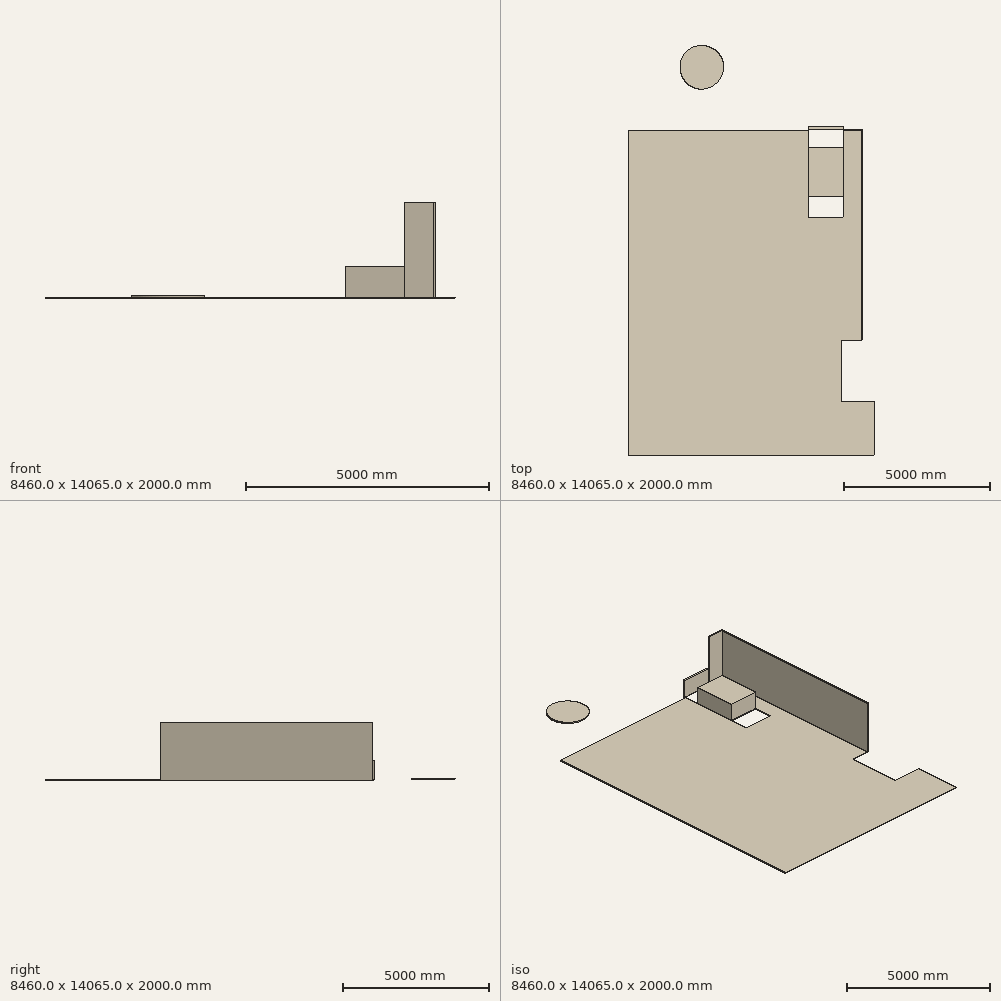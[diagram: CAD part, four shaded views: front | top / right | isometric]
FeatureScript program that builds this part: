
annotation { "Feature Type Name" : "Feature", "Feature Type Description" : "" }
export const myFeature = defineFeature(function(context is Context, id is Id, definition is map)
    precondition{}
    {
        {
            var Q0;
            Q0=qCreatedBy(makeId("Top.planeOp"),FACE);
            var sketch = newSketch(context, id + "F0", { "sketchPlane" : qUnion([Q0])});
            skLineSegment(sketch, "E0", {"start": v(3786.2, -11769.83) * mm, "end": v(3786.2, -9919.83) * mm});
            skLineSegment(sketch, "E1", {"start": v(3786.2, -9919.83) * mm, "end": v(2626.2, -9919.83) * mm});
            skLineSegment(sketch, "E2", {"start": v(2626.2, -9919.83) * mm, "end": v(2626.2, -7819.83) * mm});
            skLineSegment(sketch, "E3", {"start": v(2626.2, -7819.83) * mm, "end": v(3326.2, -7819.83) * mm});
            skLineSegment(sketch, "E4", {"start": v(3326.2, -7819.83) * mm, "end": v(3326.2, -619.83) * mm});
            skLineSegment(sketch, "E5", {"start": v(3326.2, -619.83) * mm, "end": v(-4673.8, -619.83) * mm});
            skLineSegment(sketch, "E6", {"start": v(-4673.8, -619.83) * mm, "end": v(-4673.8, -11769.83) * mm});
            skLineSegment(sketch, "E7", {"start": v(-4673.8, -11769.83) * mm, "end": v(3786.2, -11769.83) * mm});
            skLineSegment(sketch, "E8.bottom", {"start": v(2726.2, -1219.83) * mm, "end": v(1526.2, -1219.83) * mm});
            skLineSegment(sketch, "E8.top", {"start": v(2726.2, -3619.83) * mm, "end": v(1526.2, -3619.83) * mm});
            skLineSegment(sketch, "E8.left", {"start": v(2726.2, -1219.83) * mm, "end": v(2726.2, -3619.83) * mm});
            skLineSegment(sketch, "E8.right", {"start": v(1526.2, -1219.83) * mm, "end": v(1526.2, -3619.83) * mm});
            skLineSegment(sketch, "E9.bottom", {"start": v(2726.2, -492.67) * mm, "end": v(1526.2, -492.67) * mm});
            skLineSegment(sketch, "E9.top", {"start": v(2726.2, -2892.67) * mm, "end": v(1526.2, -2892.67) * mm});
            skLineSegment(sketch, "E9.left", {"start": v(2726.2, -492.67) * mm, "end": v(2726.2, -2892.67) * mm});
            skLineSegment(sketch, "E9.right", {"start": v(1526.2, -492.67) * mm, "end": v(1526.2, -2892.67) * mm});
            skLineSegment(sketch, "E10", {"start": v(-4673.8, -11769.83) * mm, "end": v(-4723.8, -11769.83) * mm});
            skLineSegment(sketch, "E11", {"start": v(-4723.8, -11769.83) * mm, "end": v(-4723.8, -569.83) * mm});
            skLineSegment(sketch, "E12", {"start": v(-4723.8, -569.83) * mm, "end": v(3376.2, -569.83) * mm});
            skLineSegment(sketch, "E13", {"start": v(3376.2, -569.83) * mm, "end": v(3376.2, -7819.83) * mm});
            skLineSegment(sketch, "E14", {"start": v(3326.2, -7819.83) * mm, "end": v(3376.2, -7819.83) * mm});
            skLineSegment(sketch, "E15", {"start": v(-4723.8, -11769.83) * mm, "end": v(-4723.8, -19894.83) * mm});
            skLineSegment(sketch, "E16", {"start": v(-4723.8, -19894.83) * mm, "end": v(-2573.8, -19894.83) * mm});
            skLineSegment(sketch, "E17", {"start": v(-2573.8, -19894.83) * mm, "end": v(-2573.8, -11769.83) * mm});
            skSolve(sketch);
        }
        {
            var Q0;
            Q0=makeQuery(id+"F0.imprint","IMPRINT",FACE,{"disambiguationData":[TD([[makeQuery(id+"F0.imprint","IMPRINT",EDGE,{"derivedFrom":sQuery(id+"F0.wireOp",EDGE,"E9.bottom")}),1.0]])]});
            var Q1;
            Q1=makeQuery(id+"F0.imprint","IMPRINT",FACE,{"disambiguationData":[TD([[makeQuery(id+"F0.imprint","IMPRINT",EDGE,{"derivedFrom":sQuery(id+"F0.wireOp",EDGE,"E8.bottom")}),1.0]])]});
            var Q2;
            Q2=makeQuery(id+"F0.imprint","IMPRINT",FACE,{"disambiguationData":[TD([[makeQuery(id+"F0.imprint","IMPRINT",EDGE,{"derivedFrom":sQuery(id+"F0.wireOp",EDGE,"E0")}),1.0]])]});
            extrude(context, id + "F1", {"entities" : qUnion([Q0, Q1, Q2]), "depth" : 25 * mm, "offsetDistance" : 25 * mm});
        }
        {
            var Q0;
            Q0=makeQuery(id+"F0.imprint","IMPRINT",FACE,{"disambiguationData":[TD([[makeQuery(id+"F0.imprint","IMPRINT",EDGE,{"derivedFrom":sQuery(id+"F0.wireOp",EDGE,"E8.bottom")}),1.0]])]});
            var Q1;
            Q1=makeQuery(id+"F0.imprint","IMPRINT",FACE,{"disambiguationData":[TD([[makeQuery(id+"F0.imprint","IMPRINT",EDGE,{"derivedFrom":sQuery(id+"F0.wireOp",EDGE,"E9.bottom")}),1.0]])]});
            extrude(context, id + "F2", {"entities" : qUnion([Q0, Q1]), "depth" : 675 * mm, "offsetDistance" : 25 * mm});
        }
        {
            var Q0;
            Q0=makeQuery(id+"F0.imprint","IMPRINT",FACE,{"disambiguationData":[TD([[makeQuery(id+"F0.imprint","IMPRINT",EDGE,{"derivedFrom":sQuery(id+"F0.wireOp",EDGE,"E4")}),-1.0]])]});
            extrude(context, id + "F3", {"entities" : qUnion([Q0]), "depth" : 2000 * mm, "offsetDistance" : 25 * mm});
        }
        {
            var Q0;
            Q0=makeQuery(id+"F1.opExtrude","CAP_FACE",FACE,{"disambiguationData":[OSD([sQuery(id+"F0.wireOp",EDGE,"E0"),sQuery(id+"F0.wireOp",EDGE,"E1"),sQuery(id+"F0.wireOp",EDGE,"E2"),sQuery(id+"F0.wireOp",EDGE,"E3"),sQuery(id+"F0.wireOp",EDGE,"E4"),sQuery(id+"F0.wireOp",EDGE,"E5"),sQuery(id+"F0.wireOp",EDGE,"E6"),sQuery(id+"F0.wireOp",EDGE,"E7")])],"isStart":false});
            var sketch = newSketch(context, id + "F4", { "sketchPlane" : qUnion([Q0])});
            skCircle(sketch, "E18", {"center": v(-2147.22, 1545.19) * mm, "radius": 750 * mm});
            skSolve(sketch);
        }
        {
            var Q0;
            Q0=qSketchRegion(id+"F4",true);
            extrude(context, id + "F5", {"entities" : qUnion([Q0]), "depth" : 50 * mm, "offsetDistance" : 25 * mm});
        }
    });
